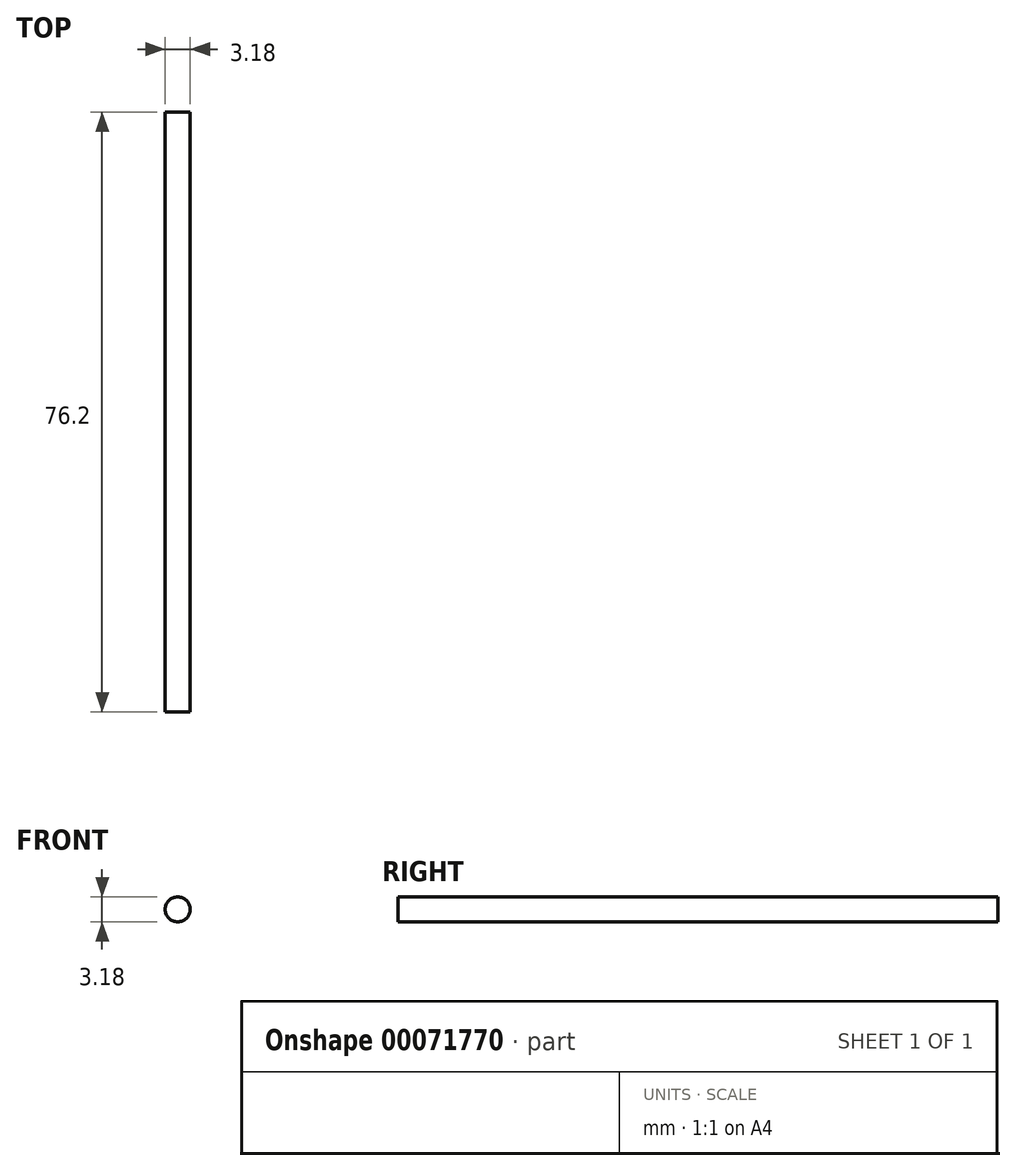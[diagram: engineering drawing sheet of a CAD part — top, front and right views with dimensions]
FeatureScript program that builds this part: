
annotation { "Feature Type Name" : "Feature", "Feature Type Description" : "" }
export const myFeature = defineFeature(function(context is Context, id is Id, definition is map)
    precondition{}
    {
        {
            var Q0;
            Q0=qCreatedBy(makeId("Front.planeOp"),FACE);
            var sketch = newSketch(context, id + "F0", { "sketchPlane" : qUnion([Q0])});
            skCircle(sketch, "E0", {"center": v(0, 0) * mm, "radius": 1.59 * mm});
            skSolve(sketch);
        }
        {
            var Q0;
            Q0 = qSketchRegion(id + "F0", true);
            extrude(context, id + "F1", {"entities" : qUnion([Q0]), "depth" : 76.2 * mm});
        }
    });
